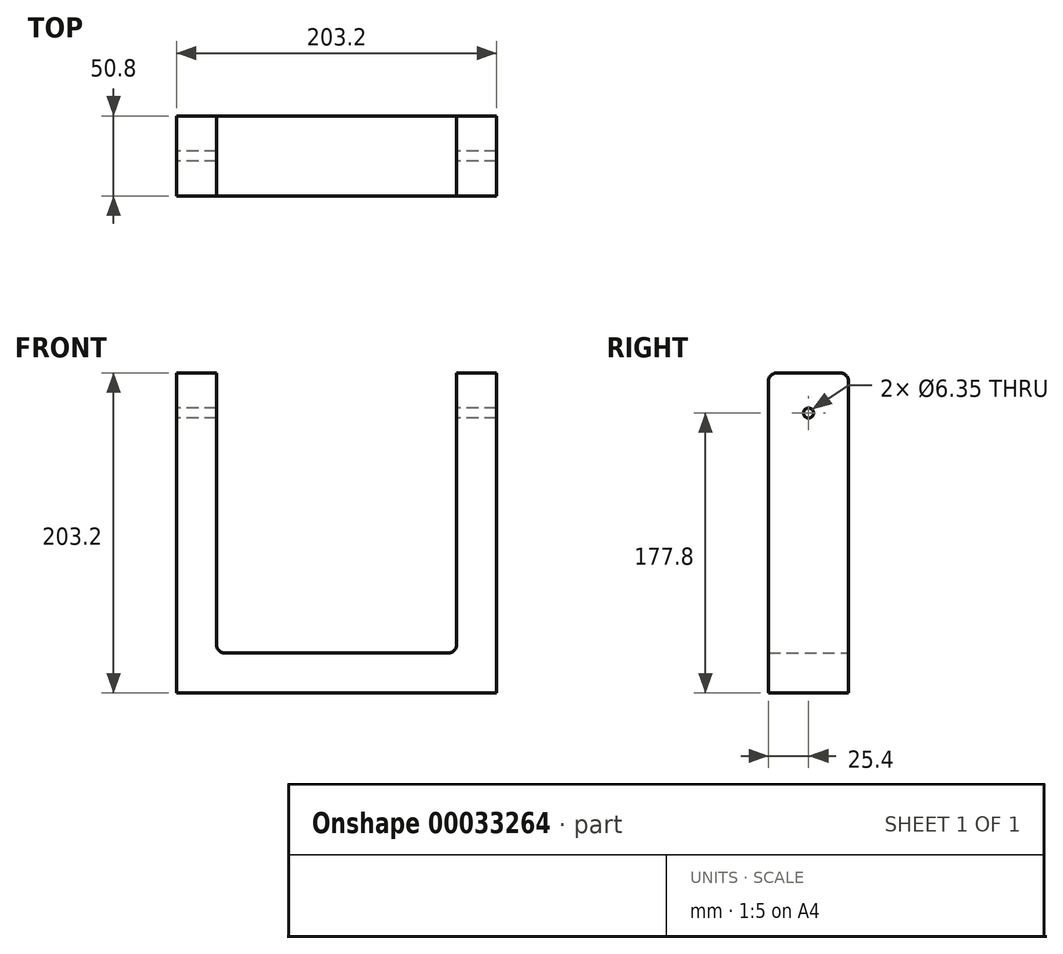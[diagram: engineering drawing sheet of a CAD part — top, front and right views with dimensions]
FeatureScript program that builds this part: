
annotation { "Feature Type Name" : "Feature", "Feature Type Description" : "" }
export const myFeature = defineFeature(function(context is Context, id is Id, definition is map)
    precondition{}
    {
        {
            var Q0;
            Q0=qCreatedBy(makeId("Front.planeOp"),FACE);
            var sketch = newSketch(context, id + "F0", { "sketchPlane" : qUnion([Q0])});
            skLineSegment(sketch, "E0.bottom", {"start": v(-101.6, 107.92) * mm, "end": v(-76.2, 107.92) * mm});
            skLineSegment(sketch, "E0.top", {"start": v(-101.6, -95.28) * mm, "end": v(101.6, -95.28) * mm});
            skLineSegment(sketch, "E0.left", {"start": v(-101.6, 107.92) * mm, "end": v(-101.6, -95.28) * mm});
            skLineSegment(sketch, "E0.right", {"start": v(101.6, 107.92) * mm, "end": v(101.6, -95.28) * mm});
            skLineSegment(sketch, "E1.top", {"start": v(-76.2, -69.88) * mm, "end": v(76.2, -69.88) * mm});
            skLineSegment(sketch, "E1.left", {"start": v(-76.2, 107.92) * mm, "end": v(-76.2, -69.88) * mm});
            skLineSegment(sketch, "E1.right", {"start": v(76.2, 107.92) * mm, "end": v(76.2, -69.88) * mm});
            skLineSegment(sketch, "E2.trimOffspring", {"start": v(76.2, 107.92) * mm, "end": v(101.6, 107.92) * mm});
            skSolve(sketch);
        }
        {
            var Q0;
            Q0 = qSketchRegion(id + "F0", true);
            extrude(context, id + "F1", {"entities" : qUnion([Q0]), "depth" : 25.4 * mm, "hasSecondDirection" : true, "secondDirectionOppositeDirection" : true, "secondDirectionDepth" : 25.4 * mm});
        }
        {
            var Q0;
            Q0=makeQuery(id+"F1.opExtrude","CAP_EDGE",EDGE,{"disambiguationData":[OSD([sQuery(id+"F0.wireOp",EDGE,"E0.bottom")])],"isStart":false});
            var Q1;
            Q1=makeQuery(id+"F1.opExtrude","CAP_EDGE",EDGE,{"disambiguationData":[OSD([sQuery(id+"F0.wireOp",EDGE,"E0.bottom")])],"isStart":true});
            var Q2;
            Q2=makeQuery(id+"F1.opExtrude","CAP_EDGE",EDGE,{"disambiguationData":[OSD([sQuery(id+"F0.wireOp",EDGE,"E2.trimOffspring")])],"isStart":false});
            var Q3;
            Q3=makeQuery(id+"F1.opExtrude","CAP_EDGE",EDGE,{"disambiguationData":[OSD([sQuery(id+"F0.wireOp",EDGE,"E2.trimOffspring")])],"isStart":true});
            var Q4;
            Q4=makeQuery(id+"F1.opExtrude","SWEPT_EDGE",EDGE,{"disambiguationData":[OSD([sQuery(id+"F0.wireOp",EDGE,"E1.top"),sQuery(id+"F0.wireOp",EDGE,"E1.left")])]});
            var Q5;
            Q5=makeQuery(id+"F1.opExtrude","SWEPT_EDGE",EDGE,{"disambiguationData":[OSD([sQuery(id+"F0.wireOp",EDGE,"E1.top"),sQuery(id+"F0.wireOp",EDGE,"E1.right")])]});
            fillet(context, id + "F2", {"entities" : qUnion([Q0, Q1, Q2, Q3, Q4, Q5]), "radius" : 5.08 * mm, "tangentPropagation" : true, "allowEdgeOverflow" : false});
        }
        {
            var Q0;
            Q0=makeQuery(id+"F1.opExtrude","SWEPT_FACE",FACE,{"disambiguationData":[OSD([sQuery(id+"F0.wireOp",EDGE,"E0.left")])]});
            var sketch = newSketch(context, id + "F3", { "sketchPlane" : qUnion([Q0])});
            skPoint(sketch, "E3", {"position": v(0, 82.52) * mm});
            skSolve(sketch);
        }
        {
            var Q0;
            Q0=sQuery(id+"F3.wireOp",VERTEX,"E3");
            var Q1;
            Q1=makeQuery(id+"F1.opExtrude","SWEPT_BODY",BODY,{"disambiguationData":[OSD([sQuery(id+"F0.wireOp",EDGE,"E0.bottom"),sQuery(id+"F0.wireOp",EDGE,"E0.top"),sQuery(id+"F0.wireOp",EDGE,"E0.left"),sQuery(id+"F0.wireOp",EDGE,"E0.right"),sQuery(id+"F0.wireOp",EDGE,"E1.top"),sQuery(id+"F0.wireOp",EDGE,"E1.left"),sQuery(id+"F0.wireOp",EDGE,"E1.right"),sQuery(id+"F0.wireOp",EDGE,"E2.trimOffspring")])]});
            hole(context, id + "F4", {"style" : HoleStyle.SIMPLE, "endStyle" : HoleEndStyle.THROUGH, "holeDiameter" : 6.35 * mm, "tappedDepth" : 12.7 * mm, "tapClearance" : 3, "locations" : qUnion([Q0]), "scope" : qUnion([Q1])});
        }
    });
